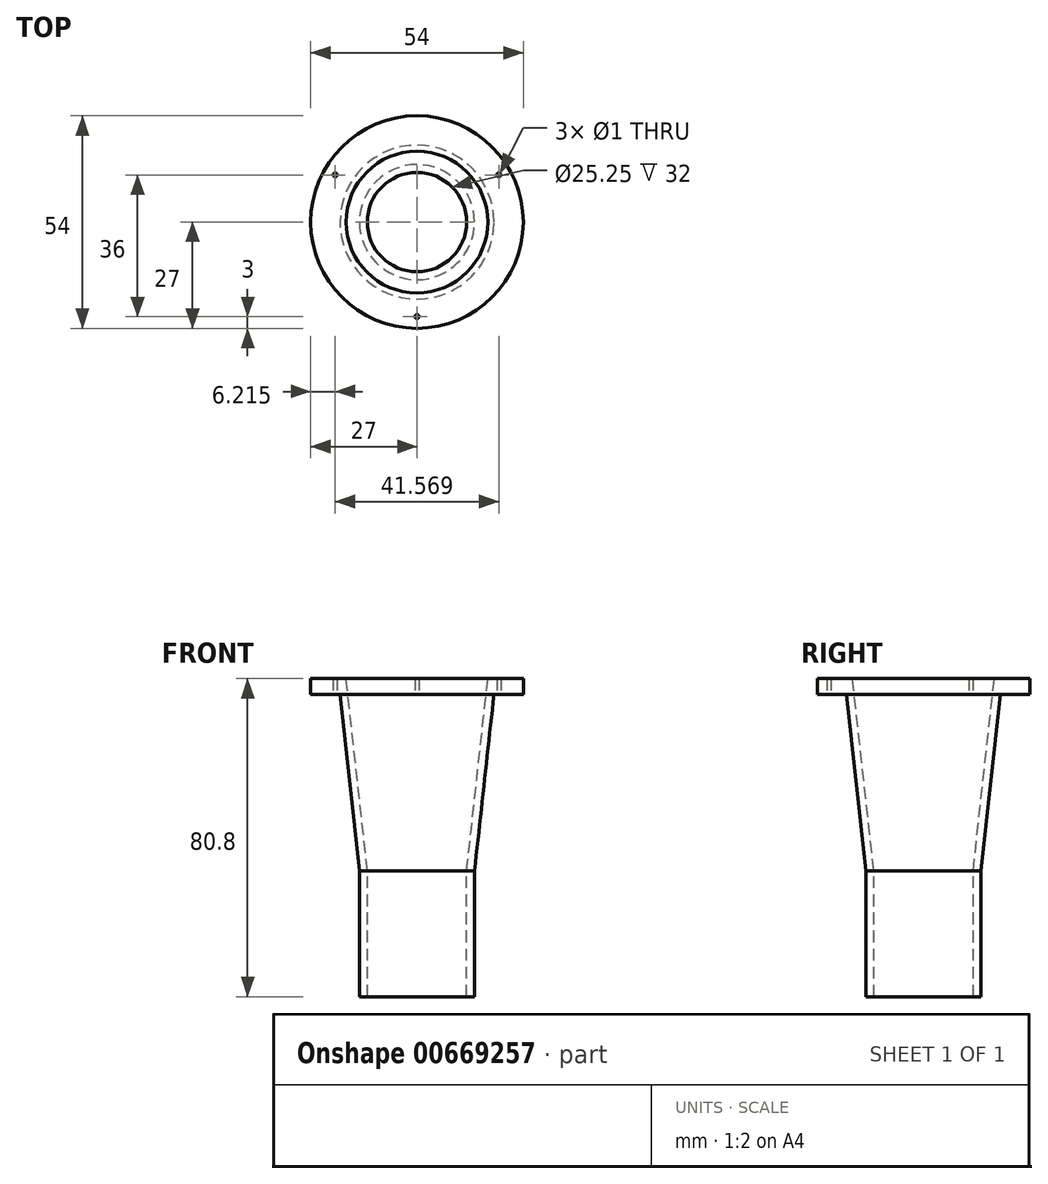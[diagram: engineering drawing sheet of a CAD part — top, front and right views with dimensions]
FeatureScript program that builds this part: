
annotation { "Feature Type Name" : "Feature", "Feature Type Description" : "" }
export const myFeature = defineFeature(function(context is Context, id is Id, definition is map)
    precondition{}
    {
        {
            var Q0;
            Q0=qCreatedBy(makeId("Top.planeOp"),FACE);
            var sketch = newSketch(context, id + "F0", { "sketchPlane" : qUnion([Q0])});
            skCircle(sketch, "E0", {"center": v(0, 0) * mm, "radius": 27 * mm});
            skCircle(sketch, "E1", {"center": v(0, 0) * mm, "radius": 18 * mm});
            skSolve(sketch);
        }
        {
            var Q0;
            Q0 = qSketchRegion(id + "F0", true);
            extrude(context, id + "F1", {"entities" : qUnion([Q0]), "oppositeDirection" : true, "depth" : 4 * mm, "offsetDistance" : 25 * mm});
        }
        {
            var Q0;
            Q0=makeQuery(id+"F1.opExtrude","CAP_FACE",FACE,{"disambiguationData":[OSD([sQuery(id+"F0.wireOp",EDGE,"E0"),sQuery(id+"F0.wireOp",EDGE,"E1")])],"isStart":true});
            var sketch = newSketch(context, id + "F2", { "sketchPlane" : qUnion([Q0])});
            skCircle(sketch, "E2.0", {"center": v(0, 0) * mm, "radius": 20 * mm});
            skSolve(sketch);
        }
        {
            var Q0;
            Q0=qCreatedBy(makeId("Top.planeOp"),FACE);
            cPlane(context, id + "F3", {"entities" : qUnion([Q0]), "cplaneType" : CPlaneType.OFFSET, "offset" : 2 * mm, "width" : 150 * mm, "height" : 150 * mm});
        }
        {
            var Q0;
            Q0=qCreatedBy(id+"F3.planeOp",FACE);
            cPlane(context, id + "F4", {"entities" : qUnion([Q0]), "cplaneType" : CPlaneType.OFFSET, "offset" : 50.8 * mm, "oppositeDirection" : true, "width" : 150 * mm, "height" : 150 * mm});
        }
        {
            var Q0;
            Q0=qCreatedBy(id+"F4.planeOp",FACE);
            var sketch = newSketch(context, id + "F5", { "sketchPlane" : qUnion([Q0])});
            skCircle(sketch, "E3", {"center": v(0, 0) * mm, "radius": 14.62 * mm});
            skSolve(sketch);
        }
        {
            var Q1;
            Q1 = qSketchRegion(id + "F2", true);
            var Q2;
            Q2 = qSketchRegion(id + "F5", true);
            loft(context, id + "F6", {"operationType" : NewBodyOperationType.ADD, "sheetProfilesArray" : [{ "sheetProfileEntities" : qUnion([Q1]) }, { "sheetProfileEntities" : qUnion([Q2]) }]});
        }
        {
            var Q0;
            {var subQ0=sQuery(id+"F0.wireOp",EDGE,"E1");Q0=makeQuery(id+"F6.boolean.opBoolean","MERGE",FACE,{"derivedFrom":[makeQuery(id+"F1.opExtrude","CAP_FACE",FACE,{"disambiguationData":[OSD([sQuery(id+"F0.wireOp",EDGE,"E0"),subQ0])],"isStart":true}),makeQuery(id+"F6.opLoft","CAP_FACE",FACE,{"disambiguationData":[OSD([makeQuery(id+"F2.imprint","IMPRINT",FACE,{"disambiguationData":[TD([[makeQuery(id+"F2.imprint","IMPRINT",EDGE,{"derivedFrom":sQuery(id+"F2.wireOp",EDGE,"E2.0")}),1.0]])]})])],"isStart":true})]});}
            var sketch = newSketch(context, id + "F7", { "sketchPlane" : qUnion([Q0])});
            skCircle(sketch, "E4", {"center": v(0, 0) * mm, "radius": 18 * mm});
            skSolve(sketch);
        }
        {
            var Q0;
            Q0=makeQuery(id+"F6.opLoft","CAP_FACE",FACE,{"disambiguationData":[OSD([makeQuery(id+"F5.imprint","IMPRINT",FACE,{"disambiguationData":[TD([[makeQuery(id+"F5.imprint","IMPRINT",EDGE,{"derivedFrom":sQuery(id+"F5.wireOp",EDGE,"E3")}),1.0]])]})])],"isStart":true});
            var sketch = newSketch(context, id + "F8", { "sketchPlane" : qUnion([Q0])});
            skCircle(sketch, "E5", {"center": v(0, 0) * mm, "radius": 12.62 * mm});
            skSolve(sketch);
        }
        {
            var Q1;
            Q1 = qSketchRegion(id + "F7", true);
            var Q2;
            Q2 = qSketchRegion(id + "F8", true);
            loft(context, id + "F9", {"operationType" : NewBodyOperationType.REMOVE, "sheetProfilesArray" : [{ "sheetProfileEntities" : qUnion([Q1]) }, { "sheetProfileEntities" : qUnion([Q2]) }]});
        }
        {
            var Q0;
            Q0=makeQuery(id+"F6.opLoft","CAP_FACE",FACE,{"disambiguationData":[OSD([makeQuery(id+"F5.imprint","IMPRINT",FACE,{"disambiguationData":[TD([[makeQuery(id+"F5.imprint","IMPRINT",EDGE,{"derivedFrom":sQuery(id+"F5.wireOp",EDGE,"E3")}),1.0]])]})])],"isStart":true});
            extrude(context, id + "F10", {"entities" : qUnion([Q0]), "operationType" : NewBodyOperationType.ADD, "depth" : 32 * mm, "offsetDistance" : 25 * mm});
        }
        {
            var Q0;
            Q0=makeQuery(id+"F1.opExtrude","CAP_FACE",FACE,{"disambiguationData":[OSD([sQuery(id+"F0.wireOp",EDGE,"E0"),sQuery(id+"F0.wireOp",EDGE,"E1")])],"isStart":false});
            var sketch = newSketch(context, id + "F11", { "sketchPlane" : qUnion([Q0])});
            skCircle(sketch, "E6", {"center": v(0, 0) * mm, "radius": 24 * mm, "construction": true});
            skCircle(sketch, "E7", {"center": v(0, 24) * mm, "radius": 0.5 * mm});
            skCircle(sketch, "E8.1.0", {"center": v(-20.78, -12) * mm, "radius": 0.5 * mm});
            skCircle(sketch, "E8.2.0", {"center": v(20.78, -12) * mm, "radius": 0.5 * mm});
            skSolve(sketch);
        }
        {
            var Q0;
            Q0 = qSketchRegion(id + "F11", true);
            extrude(context, id + "F12", {"entities" : qUnion([Q0]), "operationType" : NewBodyOperationType.REMOVE, "oppositeDirection" : true, "depth" : 25 * mm, "offsetDistance" : 25 * mm});
        }
    });
